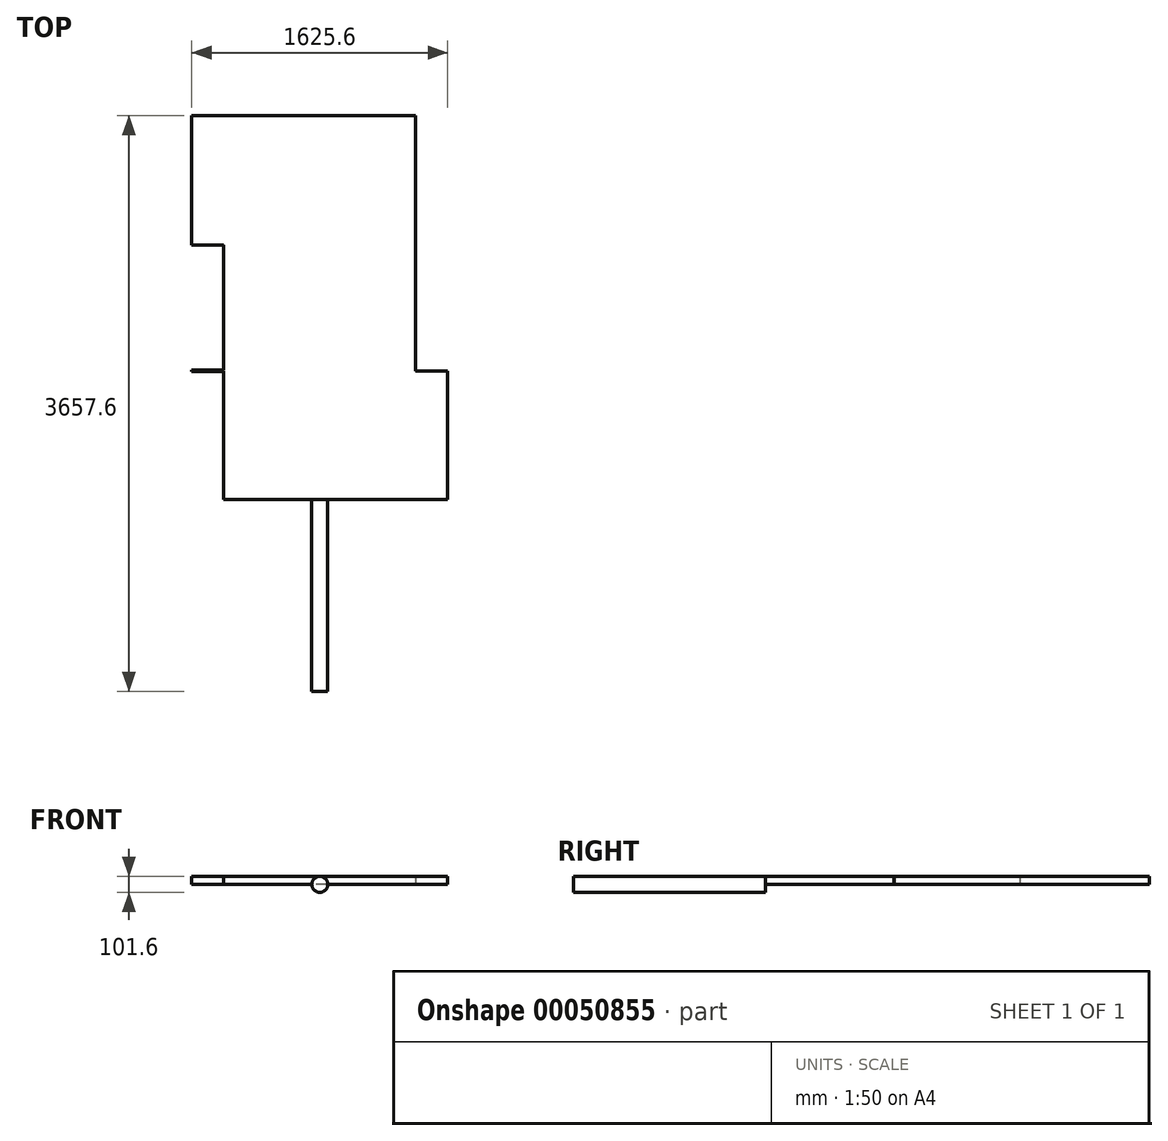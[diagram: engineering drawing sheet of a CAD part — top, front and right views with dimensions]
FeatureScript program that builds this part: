
annotation { "Feature Type Name" : "Feature", "Feature Type Description" : "" }
export const myFeature = defineFeature(function(context is Context, id is Id, definition is map)
    precondition{}
    {
        {
            var Q0;
            Q0=qCreatedBy(makeId("Top.planeOp"),FACE);
            var sketch = newSketch(context, id + "F0", { "sketchPlane" : qUnion([Q0])});
            skLineSegment(sketch, "E0.rect.bottom", {"start": v(609.6, 1219.2) * mm, "end": v(-609.6, 1219.2) * mm});
            skLineSegment(sketch, "E0.rect.top", {"start": v(609.6, -1219.2) * mm, "end": v(-609.6, -1219.2) * mm});
            skLineSegment(sketch, "E0.rect.left", {"start": v(609.6, 1219.2) * mm, "end": v(609.6, -1219.2) * mm});
            skLineSegment(sketch, "E0.rect.right", {"start": v(-609.6, 1219.2) * mm, "end": v(-609.6, -1219.2) * mm});
            skPoint(sketch, "E0.rect.middle", {"position": v(0, 0) * mm});
            skSolve(sketch);
        }
        {
            var Q0;
            Q0=makeQuery(id+"F0.imprint","IMPRINT",FACE,{"disambiguationData":[TD([[makeQuery(id+"F0.imprint","IMPRINT",EDGE,{"derivedFrom":sQuery(id+"F0.wireOp",EDGE,"E0.rect.bottom")}),1.0]])]});
            extrude(context, id + "F1", {"entities" : qUnion([Q0]), "depth" : 50.8 * mm});
        }
        {
            var Q0;
            Q0=makeQuery(id+"F1.opExtrude","SWEPT_FACE",FACE,{"disambiguationData":[OSD([sQuery(id+"F0.wireOp",EDGE,"E0.rect.left")])]});
            var sketch = newSketch(context, id + "F2", { "sketchPlane" : qUnion([Q0])});
            skPoint(sketch, "E1", {"position": v(0, 50.8) * mm});
            skLineSegment(sketch, "E2", {"start": v(0, 50.8) * mm, "end": v(330.2, 50.8) * mm});
            skLineSegment(sketch, "E3", {"start": v(0, 50.8) * mm, "end": v(-330.2, 50.8) * mm});
            skArc(sketch, "E4", {"start": v(-326.27, 0) * mm, "mid": v(0, -279.4) * mm, "end": v(326.27, 0) * mm});
            skArc(sketch, "E5.0", {"start": v(-313.4, 0) * mm, "mid": v(0, -266.7) * mm, "end": v(313.4, 0) * mm});
            skLineSegment(sketch, "E6", {"start": v(326.27, 0) * mm, "end": v(313.4, 0) * mm});
            skLineSegment(sketch, "E7.trimOffspring", {"start": v(-313.4, 0) * mm, "end": v(-326.27, 0) * mm});
            skSolve(sketch);
        }
        {
            var Q0;
            {var subQ8=sQuery(id+"F2.wireOp",EDGE,"E2");Q0=makeQuery(id+"F2.imprint","IMPRINT",FACE,{"disambiguationData":[TD([[makeQuery(id+"F2.imprint","IMPRINT",EDGE,{"derivedFrom":subQ8}),1.0]])]});}
            var sketch = newSketch(context, id + "F3", { "sketchPlane" : qUnion([Q0])});
            skArc(sketch, "E8", {"start": v(-406.4, 0) * mm, "mid": v(0, 406.4) * mm, "end": v(406.4, 0) * mm});
            skArc(sketch, "E9.0", {"start": v(-400.05, 0) * mm, "mid": v(0, 400.05) * mm, "end": v(400.05, 0) * mm});
            skSolve(sketch);
        }
        {
            var Q0;
            Q0=makeQuery(id+"F1.opExtrude","SWEPT_FACE",FACE,{"disambiguationData":[OSD([sQuery(id+"F0.wireOp",EDGE,"E0.rect.right")])]});
            var sketch = newSketch(context, id + "F4", { "sketchPlane" : qUnion([Q0])});
            skArc(sketch, "E10", {"start": v(-406.4, 0) * mm, "mid": v(0, 406.4) * mm, "end": v(406.4, 0) * mm});
            skArc(sketch, "E11.0", {"start": v(-400.05, 0) * mm, "mid": v(0, 400.05) * mm, "end": v(400.05, 0) * mm});
            skLineSegment(sketch, "E12", {"start": v(-406.4, 0) * mm, "end": v(-400.05, 0) * mm});
            skLineSegment(sketch, "E13", {"start": v(400.05, 0) * mm, "end": v(406.4, 0) * mm});
            skSolve(sketch);
        }
        {
            var Q0;
            {var subQ0=sQuery(id+"F3.wireOp",EDGE,"E8");var subQ1=sQuery(id+"F0.wireOp",EDGE,"E0.rect.left");var subQ2=makeQuery(id+"F1.opExtrude","CAP_EDGE",EDGE,{"disambiguationData":[OSD([subQ1])],"isStart":false});var subQ3=makeQuery(id+"F2.imprint","IMPRINT",EDGE,{"disambiguationData":[TD([[makeQuery(id+"F2.imprint","INTERSECT",VERTEX,{"derivedFrom":[subQ2,sQuery(id+"F2.wireOp",EDGE,"E3")]}),-1.0]])],"derivedFrom":subQ2});var subQ4=makeQuery(id+"F3.imprint","INTERSECT",VERTEX,{"derivedFrom":[subQ3,subQ0]});Q0=makeQuery(id+"F3.imprint","IMPRINT",FACE,{"disambiguationData":[TD([[makeQuery(id+"F3.imprint","IMPRINT",EDGE,{"disambiguationData":[TD([[subQ4,-1.0]])],"derivedFrom":subQ0}),-1.0]])]});}
            var Q1;
            {var subQ0=sQuery(id+"F3.wireOp",EDGE,"E8");var subQ1=sQuery(id+"F0.wireOp",EDGE,"E0.rect.left");var subQ6=makeQuery(id+"F1.opExtrude","CAP_EDGE",EDGE,{"disambiguationData":[OSD([subQ1])],"isStart":false});var subQ7=makeQuery(id+"F2.imprint","IMPRINT",EDGE,{"disambiguationData":[TD([[makeQuery(id+"F2.imprint","INTERSECT",VERTEX,{"derivedFrom":[subQ6,sQuery(id+"F2.wireOp",EDGE,"E3")]}),-1.0]])],"derivedFrom":subQ6});var subQ8=makeQuery(id+"F3.imprint","INTERSECT",VERTEX,{"derivedFrom":[subQ7,subQ0]});Q1=makeQuery(id+"F3.imprint","IMPRINT",FACE,{"disambiguationData":[TD([[makeQuery(id+"F3.imprint","IMPRINT",EDGE,{"disambiguationData":[TD([[subQ8,1.0]])],"derivedFrom":subQ0}),-1.0]])]});}
            var Q2;
            {var subQ0=sQuery(id+"F3.wireOp",EDGE,"E8");var subQ1=sQuery(id+"F0.wireOp",EDGE,"E0.rect.left");var subQ6=makeQuery(id+"F1.opExtrude","CAP_EDGE",EDGE,{"disambiguationData":[OSD([subQ1])],"isStart":false});var subQ7=makeQuery(id+"F2.imprint","IMPRINT",EDGE,{"disambiguationData":[TD([[makeQuery(id+"F2.imprint","INTERSECT",VERTEX,{"derivedFrom":[subQ6,sQuery(id+"F2.wireOp",EDGE,"E2")]}),1.0]])],"derivedFrom":subQ6});var subQ8=makeQuery(id+"F3.imprint","INTERSECT",VERTEX,{"derivedFrom":[subQ7,subQ0]});Q2=makeQuery(id+"F3.imprint","IMPRINT",FACE,{"disambiguationData":[TD([[makeQuery(id+"F3.imprint","IMPRINT",EDGE,{"disambiguationData":[TD([[subQ8,-1.0]])],"derivedFrom":subQ0}),-1.0]])]});}
            var Q3;
            Q3=sQuery(id+"F3.wireOp",EDGE,"E9.0");
            extrude(context, id + "F5", {"entities" : qUnion([Q0, Q1, Q2]), "operationType" : NewBodyOperationType.ADD, "surfaceEntities" : qUnion([Q3]), "depth" : 203.2 * mm});
        }
        {
            var Q0;
            {var subQ0=sQuery(id+"F4.wireOp",EDGE,"E10");var subQ1=makeQuery(id+"F1.opExtrude","CAP_EDGE",EDGE,{"disambiguationData":[OSD([sQuery(id+"F0.wireOp",EDGE,"E0.rect.right")])],"isStart":false});var subQ2=makeQuery(id+"F4.imprint","INTERSECT",VERTEX,{"disambiguationData":[OD(0.0)],"derivedFrom":[subQ1,subQ0]});Q0=makeQuery(id+"F4.imprint","IMPRINT",FACE,{"disambiguationData":[TD([[makeQuery(id+"F4.imprint","IMPRINT",EDGE,{"disambiguationData":[TD([[subQ2,-1.0]])],"derivedFrom":subQ0}),-1.0]])]});}
            var Q1;
            {var subQ0=sQuery(id+"F4.wireOp",EDGE,"E13");Q1=makeQuery(id+"F4.imprint","IMPRINT",FACE,{"disambiguationData":[TD([[makeQuery(id+"F4.imprint","IMPRINT",EDGE,{"derivedFrom":subQ0}),1.0]])]});}
            var Q2;
            {var subQ0=sQuery(id+"F4.wireOp",EDGE,"E12");Q2=makeQuery(id+"F4.imprint","IMPRINT",FACE,{"disambiguationData":[TD([[makeQuery(id+"F4.imprint","IMPRINT",EDGE,{"derivedFrom":subQ0}),1.0]])]});}
            var Q3;
            Q3=sQuery(id+"F4.wireOp",EDGE,"E11.0");
            extrude(context, id + "F6", {"entities" : qUnion([Q0, Q1, Q2]), "operationType" : NewBodyOperationType.ADD, "surfaceEntities" : qUnion([Q3]), "depth" : 203.2 * mm});
        }
        {
            var Q0;
            Q0=makeQuery(id+"F1.opExtrude","SWEPT_FACE",FACE,{"disambiguationData":[OSD([sQuery(id+"F0.wireOp",EDGE,"E0.rect.top")])]});
            var sketch = newSketch(context, id + "F7", { "sketchPlane" : qUnion([Q0])});
            skCircle(sketch, "E14", {"center": v(0, 0) * mm, "radius": 50.8 * mm});
            skSolve(sketch);
        }
        {
            var Q0;
            {var subQ0=sQuery(id+"F7.wireOp",EDGE,"E14");var subQ1=sQuery(id+"F0.wireOp",EDGE,"E0.rect.top");var subQ2=makeQuery(id+"F7.imprint","INTERSECT",VERTEX,{"derivedFrom":[makeQuery(id+"F1.opExtrude","CAP_EDGE",EDGE,{"disambiguationData":[OSD([subQ1])],"isStart":false}),subQ0]});Q0=makeQuery(id+"F7.imprint","IMPRINT",FACE,{"disambiguationData":[TD([[makeQuery(id+"F7.imprint","IMPRINT",EDGE,{"disambiguationData":[TD([[subQ2,1.0]])],"derivedFrom":subQ0}),1.0]])]});}
            var Q1;
            {var subQ0=sQuery(id+"F7.wireOp",EDGE,"E14");var subQ1=makeQuery(id+"F1.opExtrude","CAP_EDGE",EDGE,{"disambiguationData":[OSD([sQuery(id+"F0.wireOp",EDGE,"E0.rect.top")])],"isStart":true});var subQ2=makeQuery(id+"F7.imprint","INTERSECT",VERTEX,{"disambiguationData":[OD(0.0)],"derivedFrom":[subQ1,subQ0]});Q1=makeQuery(id+"F7.imprint","IMPRINT",FACE,{"disambiguationData":[TD([[makeQuery(id+"F7.imprint","IMPRINT",EDGE,{"disambiguationData":[TD([[subQ2,1.0]])],"derivedFrom":subQ0}),1.0]])]});}
            extrude(context, id + "F8", {"entities" : qUnion([Q0, Q1]), "operationType" : NewBodyOperationType.ADD, "depth" : 1219.2 * mm});
        }
    });
